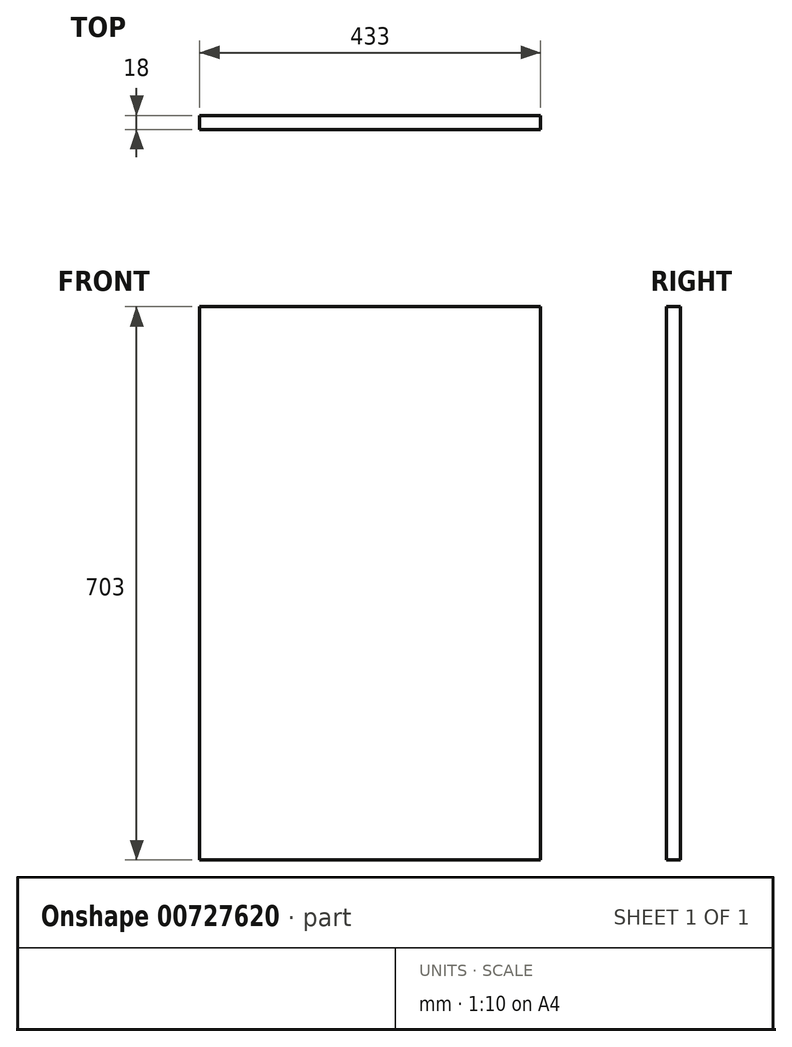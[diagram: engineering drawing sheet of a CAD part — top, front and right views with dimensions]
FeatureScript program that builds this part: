
annotation { "Feature Type Name" : "Feature", "Feature Type Description" : "" }
export const myFeature = defineFeature(function(context is Context, id is Id, definition is map)
    precondition{}
    {
        {
            var Q0;
            Q0=qCreatedBy(makeId("Front.planeOp"),FACE);
            var sketch = newSketch(context, id + "F0", { "sketchPlane" : qUnion([Q0])});
            skLineSegment(sketch, "E0.bottom", {"start": v(-216.5, 351.5) * mm, "end": v(216.5, 351.5) * mm});
            skLineSegment(sketch, "E0.top", {"start": v(-216.5, -351.5) * mm, "end": v(216.5, -351.5) * mm});
            skLineSegment(sketch, "E0.left", {"start": v(-216.5, 351.5) * mm, "end": v(-216.5, -351.5) * mm});
            skLineSegment(sketch, "E0.right", {"start": v(216.5, 351.5) * mm, "end": v(216.5, -351.5) * mm});
            skLineSegment(sketch, "E1", {"start": v(-216.5, 351.5) * mm, "end": v(216.5, -351.5) * mm, "construction": true});
            skSolve(sketch);
        }
        {
            var Q0;
            Q0 = qSketchRegion(id + "F0", true);
            extrude(context, id + "F1", {"entities" : qUnion([Q0]), "oppositeDirection" : true, "depth" : 18 * mm, "offsetDistance" : 25 * mm});
        }
    });
